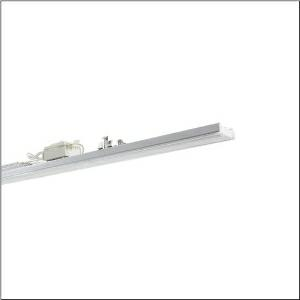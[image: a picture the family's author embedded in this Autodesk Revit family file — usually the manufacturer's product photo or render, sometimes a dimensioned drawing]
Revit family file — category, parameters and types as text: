
# Revit family: licross_r__21_recessed_mo_51te11vn48xg_21ab
name_source: partatom
category: Lighting Fixtures
units: mm (PartAtom-declared; Revit-internal decimal feet)

## family parameters
Cut with Voids When Loaded = No
Host = Face
Light Source = No
Part Type = Normal
Room Calculation Point = No
Round Connector Dimension = Use Diameter
Shared = No

## types (1)
- --- (1 x LED, 8000 lm, 44.1 W, 4000K)
    Apparent Load = 44 VA
    CIE Flux Codes = 89 96 99 100 100
    Color Rendering = 80
    Color Temperature = 4000K
    Default Elevation = 1800 mm
    Description = Licross® 21 Recessed MO, luminaire insert, of sheet steel, galvanised, coil coated, white, length: 1.500mm, width: 66mm, height: 67mm, LED rated luminous flux: 8.000lm, light colour: 840, control gear: DALI 2, CLO, with plug, 5-pole, with phase selection, mains connection: 220..240V, AC, 50/60Hz, start of lifetime: 44W, end of service life: 48W, internal wiring halogen-free, primary light control with lens, of plastic, primary optical cover: cover, of PMMA, light emission: direct distribution, primary light characteristic: symmetric, protection rating (complete): IP54, insulation class (complete): insulation class I (protective earthing), certification: CE, ENEC, VDE, UKCA, protection symbol: D if used in an environment with non-conductive dust loads with corresponding accessories, impact resistance: IK06, permissible ambient temperature for indoor applications: -25..+35°C, corresponds to IFS (International Featured Standards) requirements for safety and quality in the food industry, reducing of maximum allowable ambient temperature of 5°C with ceiling mounting, LABS conformity tested according to VDMA 24364:2018-05, packaging unit: 1 piece
    Height = 58 mm
    Lamp = 1 x LED
    Lamp Light Flux = 8000 lm
    Lamp Power = 44.1 W
    Lamp count = 1
    Length = 1500 mm
    Luminous efficacy = 181 lm/W
    Manufacturer = Siteco
    ModVariant = No
    Model = 51TE11VN48XG
    Mounting Place = Ceiling
    Mounting Type = Pendant
    Number of Poles = 1
    OnlyDefault = Yes
    Power Factor = 1
    Product Name = Licross® 21 Recessed MO
    Product group = luminaire insert | ceiling pendant
    ProductGroupID = 902
    Protection Class = Protection class I
    Protection Degree = IP 54
    RLX_Detail_Level = 1
    RLX_Emergency_Light_Flux = 0 lm
    RLX_Emergency_Type = 0
    RLX_Emergency_Type_DB = No
    RlxData = <blob elided: 24597 chars, md5=911709d8>
    Socket = socket
    Standby Power = 0 W
    System Light Flux = 8000 lm
    System Power = 44 W
    Type Comments = factory setting: luminous flux: 100 % | dim-lin: 254 | 294 mA
    Type Image = l_1296930.jpg
    URL = http://relux.com
    VarID = @adj_108409
    Voltage = 0 V
    Weight = 0.00 kg
    Width = 66 mm

## geometry (parser evidence)
native form markers: Blend x4, Sweep x11
no freeform markers — native parametric forms only
